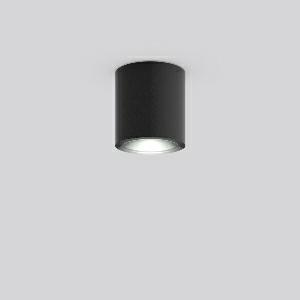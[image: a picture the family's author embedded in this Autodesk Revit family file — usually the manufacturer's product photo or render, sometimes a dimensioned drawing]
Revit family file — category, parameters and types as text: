
# Revit family: hb_110_931186_0031_d527
name_source: partatom
category: Lighting Fixtures
units: mm (PartAtom-declared; Revit-internal decimal feet)

## family parameters
Cut with Voids When Loaded = No
Host = Face
Light Source = No
Part Type = Normal
Room Calculation Point = No
Round Connector Dimension = Use Diameter
Shared = No

## types (1)
- HB 110 (1 x LED Modul 830, 570 lm, 3000)
    Apparent Load = 9 VA
    CIE Flux Codes = 71 98 100 98 99
    Color Rendering = 80
    Color Temperature = 3000
    Default Elevation = 1800 mm
    Description = Series: HB 110
Round surface-mounted downlight for outdoor use. Housing: die-cast aluminium, powder-coated. Clear glass cover. Driver integrated. 
Colour: anthracite metallic (DB703)
Diameter: 90 mm
Height: 95 mm
Lamp: LED
System power: 9 W
Rated luminous flux: 570 lm
Luminous efficiency: 63 lm/W
Control gear: Regulated power supply
Protection class: I
Type of protection: IP 54
    Height = 95 mm
    Lamp = 1 x LED Modul 830
    Lamp Light Flux = 570 lm
    Lamp count = 1
    Length = 90 mm
    Lifetime = 50000 h
    Luminous efficacy = 63 lm/W
    Manufacturer = RZB
    ModVariant = No
    Model = 931186.0031
    Mounting Place = Ceiling
    Mounting Type = Surface mounted
    Number of Poles = 1
    OnlyDefault = Yes
    Power Factor = 1
    Product Name = HB 110
    Product group = Surface mounted ceiling luminaires
    ProductGroupID = 303
    Protection Class = Protection class I
    Protection Degree = IP 54
    RLX_Detail_Level = 1
    RLX_Emergency_Light_Flux = 0 lm
    RLX_Emergency_Type = 0
    RLX_Emergency_Type_DB = No
    RlxData = <blob elided: 27837 chars, md5=2ecb8596>
    Socket = socket
    Standby Power = 0 W
    System Light Flux = 570 lm
    System Power = 9 W
    Type Comments = Product without accessories
    Type Image = 931186.0031.jpg
    URL = http://relux.com
    VarID = ---
    Voltage = 230 V
    Voltage Range = 220-240 V
    Weight = 0.00 kg
    Width = 0 mm  [stored 0 ft]

note: [stored X ft] marks values corroborated as IEEE doubles in the binary element streams (Revit-internal decimal feet)

## geometry (parser evidence)
native form markers: Blend x4, Sweep x10
no freeform markers — native parametric forms only
